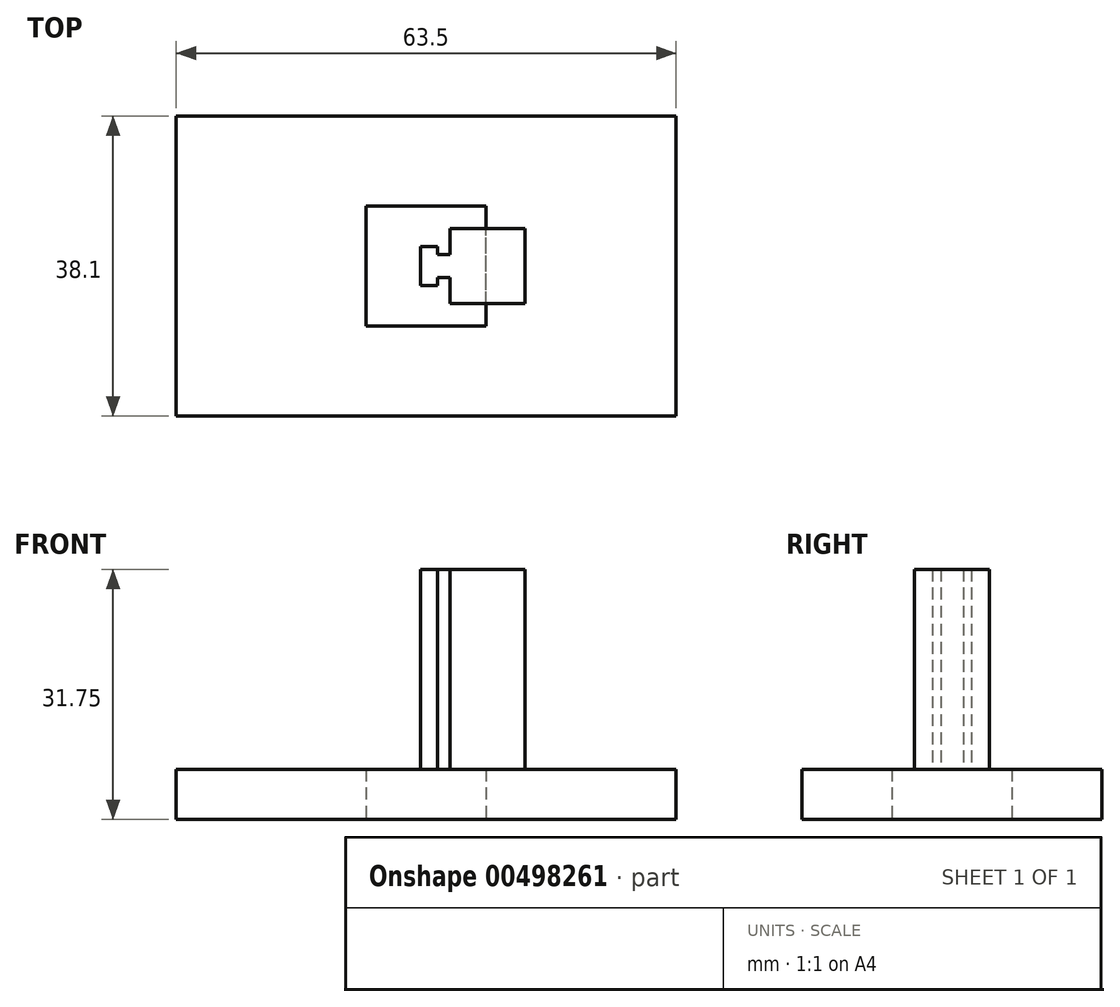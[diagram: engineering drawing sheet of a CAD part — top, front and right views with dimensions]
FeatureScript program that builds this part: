
annotation { "Feature Type Name" : "Feature", "Feature Type Description" : "" }
export const myFeature = defineFeature(function(context is Context, id is Id, definition is map)
    precondition{}
    {
        {
            var Q0;
            Q0=qCreatedBy(makeId("Top.planeOp"),FACE);
            var sketch = newSketch(context, id + "F0", { "sketchPlane" : qUnion([Q0])});
            skLineSegment(sketch, "E0.bottom", {"start": v(0, 0) * mm, "end": v(63.5, 0) * mm});
            skLineSegment(sketch, "E0.top", {"start": v(0, -38.1) * mm, "end": v(63.5, -38.1) * mm});
            skLineSegment(sketch, "E0.left", {"start": v(0, 0) * mm, "end": v(0, -38.1) * mm});
            skLineSegment(sketch, "E0.right", {"start": v(63.5, 0) * mm, "end": v(63.5, -38.1) * mm});
            skSolve(sketch);
        }
        {
            var Q0;
            Q0=makeQuery(id+"F0.imprint","IMPRINT",FACE,{"disambiguationData":[TD([[makeQuery(id+"F0.imprint","IMPRINT",EDGE,{"derivedFrom":sQuery(id+"F0.wireOp",EDGE,"E0.bottom")}),-1.0]])]});
            extrude(context, id + "F1", {"entities" : qUnion([Q0]), "depth" : 6.35 * mm});
        }
        {
            var Q0;
            Q0=makeQuery(id+"F1.opExtrude","CAP_FACE",FACE,{"disambiguationData":[OSD([sQuery(id+"F0.wireOp",EDGE,"E0.bottom"),sQuery(id+"F0.wireOp",EDGE,"E0.top"),sQuery(id+"F0.wireOp",EDGE,"E0.left"),sQuery(id+"F0.wireOp",EDGE,"E0.right")])],"isStart":false});
            var sketch = newSketch(context, id + "F2", { "sketchPlane" : qUnion([Q0])});
            skLineSegment(sketch, "E1", {"start": v(31.75, 0) * mm, "end": v(31.75, -38.1) * mm});
            skLineSegment(sketch, "E2", {"start": v(0, -19.05) * mm, "end": v(63.5, -19.05) * mm});
            skLineSegment(sketch, "E3", {"start": v(34.78, -17.62) * mm, "end": v(34.78, -14.29) * mm});
            skLineSegment(sketch, "E4", {"start": v(34.78, -14.29) * mm, "end": v(44.3, -14.29) * mm});
            skLineSegment(sketch, "E5", {"start": v(44.3, -14.29) * mm, "end": v(44.3, -19.05) * mm});
            skLineSegment(sketch, "E6", {"start": v(34.78, -17.62) * mm, "end": v(33.17, -17.62) * mm});
            skLineSegment(sketch, "E7", {"start": v(33.17, -17.62) * mm, "end": v(33.17, -16.57) * mm});
            skLineSegment(sketch, "E8", {"start": v(33.17, -16.57) * mm, "end": v(31.01, -16.57) * mm});
            skLineSegment(sketch, "E9", {"start": v(31.01, -16.57) * mm, "end": v(31.01, -19.05) * mm});
            skLineSegment(sketch, "E10.MirrorCS", {"start": v(44.3, -23.81) * mm, "end": v(44.3, -19.05) * mm});
            skLineSegment(sketch, "E11.MirrorCS", {"start": v(34.78, -23.81) * mm, "end": v(44.3, -23.81) * mm});
            skLineSegment(sketch, "E12.MirrorCS", {"start": v(34.78, -20.48) * mm, "end": v(34.78, -23.81) * mm});
            skLineSegment(sketch, "E13.MirrorCS", {"start": v(34.78, -20.48) * mm, "end": v(33.17, -20.48) * mm});
            skLineSegment(sketch, "E14.MirrorCS", {"start": v(33.17, -20.48) * mm, "end": v(33.17, -21.53) * mm});
            skLineSegment(sketch, "E15.MirrorCS", {"start": v(33.17, -21.53) * mm, "end": v(31.01, -21.53) * mm});
            skLineSegment(sketch, "E16.MirrorCS", {"start": v(31.01, -21.53) * mm, "end": v(31.01, -19.05) * mm});
            skSolve(sketch);
        }
        {
            var Q0;
            {var subQ5=sQuery(id+"F2.wireOp",EDGE,"E9");Q0=makeQuery(id+"F2.imprint","IMPRINT",FACE,{"disambiguationData":[TD([[makeQuery(id+"F2.imprint","IMPRINT",EDGE,{"derivedFrom":subQ5}),1.0]])]});}
            var Q1;
            Q1=makeQuery(id+"F2.imprint","IMPRINT",FACE,{"disambiguationData":[TD([[makeQuery(id+"F2.imprint","IMPRINT",EDGE,{"derivedFrom":sQuery(id+"F2.wireOp",EDGE,"E3")}),-1.0]])]});
            var Q2;
            {var subQ5=sQuery(id+"F2.wireOp",EDGE,"E16.MirrorCS");Q2=makeQuery(id+"F2.imprint","IMPRINT",FACE,{"disambiguationData":[TD([[makeQuery(id+"F2.imprint","IMPRINT",EDGE,{"derivedFrom":subQ5}),-1.0]])]});}
            var Q3;
            {var subQ0=sQuery(id+"F2.wireOp",EDGE,"E10.MirrorCS");Q3=makeQuery(id+"F2.imprint","IMPRINT",FACE,{"disambiguationData":[TD([[makeQuery(id+"F2.imprint","IMPRINT",EDGE,{"derivedFrom":subQ0}),1.0]])]});}
            extrude(context, id + "F3", {"entities" : qUnion([Q0, Q1, Q2, Q3]), "operationType" : NewBodyOperationType.ADD, "depth" : 25.4 * mm});
        }
        {
            var Q0;
            Q0=makeQuery(id+"F1.opExtrude","CAP_FACE",FACE,{"disambiguationData":[OSD([sQuery(id+"F0.wireOp",EDGE,"E0.bottom"),sQuery(id+"F0.wireOp",EDGE,"E0.top"),sQuery(id+"F0.wireOp",EDGE,"E0.left"),sQuery(id+"F0.wireOp",EDGE,"E0.right")])],"isStart":true});
            var sketch = newSketch(context, id + "F4", { "sketchPlane" : qUnion([Q0])});
            skLineSegment(sketch, "E17", {"start": v(31.75, 38.1) * mm, "end": v(31.75, 0) * mm});
            skLineSegment(sketch, "E18", {"start": v(0, 19.05) * mm, "end": v(63.5, 19.05) * mm});
            skLineSegment(sketch, "E19", {"start": v(24.13, 19.05) * mm, "end": v(24.13, 26.67) * mm});
            skLineSegment(sketch, "E20", {"start": v(24.13, 26.67) * mm, "end": v(31.75, 26.67) * mm});
            skLineSegment(sketch, "E21.MirrorCS", {"start": v(39.37, 26.67) * mm, "end": v(31.75, 26.67) * mm});
            skLineSegment(sketch, "E22.MirrorCS", {"start": v(39.37, 19.05) * mm, "end": v(39.37, 26.67) * mm});
            skLineSegment(sketch, "E23.MirrorCS", {"start": v(39.37, 19.05) * mm, "end": v(39.37, 11.43) * mm});
            skLineSegment(sketch, "E24.MirrorCS", {"start": v(39.37, 11.43) * mm, "end": v(31.75, 11.43) * mm});
            skLineSegment(sketch, "E25.MirrorCS", {"start": v(24.13, 19.05) * mm, "end": v(24.13, 11.43) * mm});
            skLineSegment(sketch, "E26.MirrorCS", {"start": v(24.13, 11.43) * mm, "end": v(31.75, 11.43) * mm});
            skSolve(sketch);
        }
        {
            var Q0;
            {var subQ4=sQuery(id+"F4.wireOp",EDGE,"E25.MirrorCS");Q0=makeQuery(id+"F4.imprint","IMPRINT",FACE,{"disambiguationData":[TD([[makeQuery(id+"F4.imprint","IMPRINT",EDGE,{"derivedFrom":subQ4}),1.0]])]});}
            var Q1;
            {var subQ4=sQuery(id+"F4.wireOp",EDGE,"E23.MirrorCS");Q1=makeQuery(id+"F4.imprint","IMPRINT",FACE,{"disambiguationData":[TD([[makeQuery(id+"F4.imprint","IMPRINT",EDGE,{"derivedFrom":subQ4}),-1.0]])]});}
            var Q2;
            {var subQ0=sQuery(id+"F4.wireOp",EDGE,"E21.MirrorCS");Q2=makeQuery(id+"F4.imprint","IMPRINT",FACE,{"disambiguationData":[TD([[makeQuery(id+"F4.imprint","IMPRINT",EDGE,{"derivedFrom":subQ0}),1.0]])]});}
            var Q3;
            {var subQ4=sQuery(id+"F4.wireOp",EDGE,"E19");Q3=makeQuery(id+"F4.imprint","IMPRINT",FACE,{"disambiguationData":[TD([[makeQuery(id+"F4.imprint","IMPRINT",EDGE,{"derivedFrom":subQ4}),-1.0]])]});}
            extrude(context, id + "F5", {"entities" : qUnion([Q0, Q1, Q2, Q3]), "operationType" : NewBodyOperationType.REMOVE, "oppositeDirection" : true, "depth" : 6.35 * mm});
        }
    });
